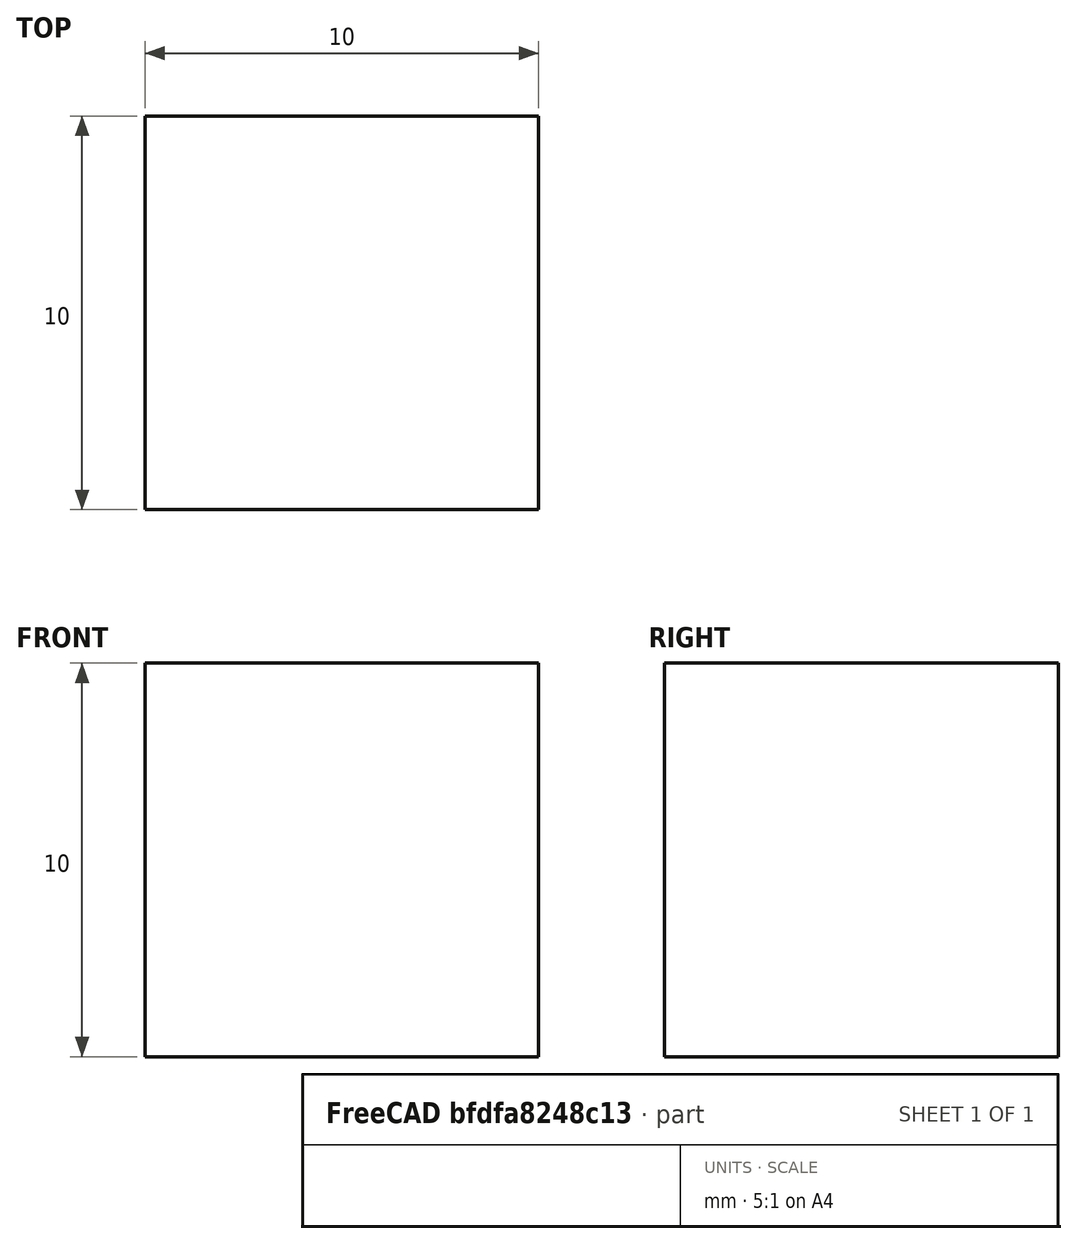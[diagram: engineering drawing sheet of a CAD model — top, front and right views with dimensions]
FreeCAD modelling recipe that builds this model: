
FCSTD DOCUMENT  (FreeCAD 1.0R39109 (Git))
Label: cube_10mm
License: All rights reserved
LicenseURL: https://en.wikipedia.org/wiki/All_rights_reserved
objects: Sketcher::SketchObject×1, PartDesign::Pad×1, PartDesign::Body×1
note: 6 computed .brp shape members not serialized (recipe doc carries the construction recipe); baked Part::Feature solids carry a one-line shape summary decoded from their .brp

FEATURE [Sketcher::SketchObject] Sketch
  ArcFitTolerance = 1e-06
  AttachmentSupport = -> [XY_Plane]
  FullyConstrained = true
  MakeInternals = false
  MapMode = 5
  sketch-geometry (4):
    g0: LineSegment StartX=0 StartY=0 StartZ=0 EndX=10 EndY=0 EndZ=0
    g1: LineSegment StartX=10 StartY=0 StartZ=0 EndX=10 EndY=10 EndZ=0
    g2: LineSegment StartX=10 StartY=10 StartZ=0 EndX=0 EndY=10 EndZ=0
    g3: LineSegment StartX=0 StartY=10 StartZ=0 EndX=0 EndY=0 EndZ=0
  constraints (11):
    c: Coincident(g0,g1)
    c: Coincident(g1,g2)
    c: Coincident(g2,g3)
    c: Coincident(g3,g0)
    c: Horizontal(g0)
    c: Horizontal(g2)
    c: Vertical(g1)
    c: Vertical(g3)
    c: Distance(g1,g3) = 10
    c: Distance(g0,g2) = 10
    c: Coincident(g0,g-1)
FEATURE [PartDesign::Pad] Pad
  Direction = (0,0,1)
  Length = 10
  Length2 = 10
  Profile = -> Sketch
  ReferenceAxis = -> Sketch [N_Axis]
  Refine = true
  Suppressed = false
  Type = 0
FEATURE [PartDesign::Body] Body
  AllowCompound = false
  Group = -> [Sketch,Pad]
  Origin = -> Origin
  Tip = -> Pad
